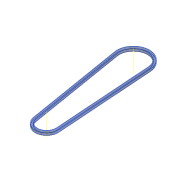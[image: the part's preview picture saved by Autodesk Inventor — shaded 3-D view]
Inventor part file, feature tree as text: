
AUTODESK INVENTOR PART (.ipt)
format: ipt  version: 2013 (Build 170138000, 138)  size: 157,696 bytes
history: native  units: mm
features: other x5, plane x2, pattern_linear x1
ambient origin geometry x8: Origin, YZ Plane, XZ Plane, XY Plane, X Axis, Y Axis, Z Axis, Center Point
bodies: Solid1 (feature_tree), Solid (feature_tree)
feature tree (8):
  other  "Work Axis1"
  other  "Work Axis2"
  plane  "Work Plane2"
  plane  "Work Plane3"
  other  "Path"
  other  "Section Plane"
  pattern_linear  "Strand Pattern"  Spacing1=0.0mm  [1 undecoded]
  other  "Section Sketch"
note: 1 required parameter value undecoded (feature->parameter linkage not recoverable at this tier; creation-order binding heuristic only, values carry confidence <= 0.55)
